# Revit family: BuzziTrom
name_source: partatom
category: Lighting Fixtures
revit_build: Autodesk Revit 2018 (Build: 20190510_1515(x64)
units: mm (PartAtom-declared; Revit-internal decimal feet)

## family parameters
Always vertical = Yes
Cut with Voids When Loaded = No
Host = Ceiling
Light Source = Yes
OmniClass Number = 23.80.70.11
OmniClass Title = Luminaries for Internal Lighting
Part Type = Normal
Room Calculation Point = No
Round Connector Dimension = Use Diameter
Shared = No

## types (6) — shared parameters
Color Filter = 16777215
Dimming Lamp Color Temperature Shift = <None>
Housing = <By Category>
Lens = <By Category>
Light Source Symbol Size = 2' - 0"
Shade = <By Category>
Stitching = <By Category>
Support = <By Category>
Suspension Length = 3' - 8 3/8"

## per-type parameters (varying)
| type | Lamp Type | Support Type |
| BuzziTrom L Split | Shade : L | split |
| BuzziTrom M Split | Shade : M | split |
| BuzziTrom S Split | Shade : S | split |
| BuzziTrom L Straight | Shade : L | split : Straight |
| BuzziTrom M Straight | Shade : M | split : Straight |
| BuzziTrom S Straight | Shade : S | split : Straight |

## geometry (parser evidence)
native form markers: Sweep x13
no freeform markers — native parametric forms only
